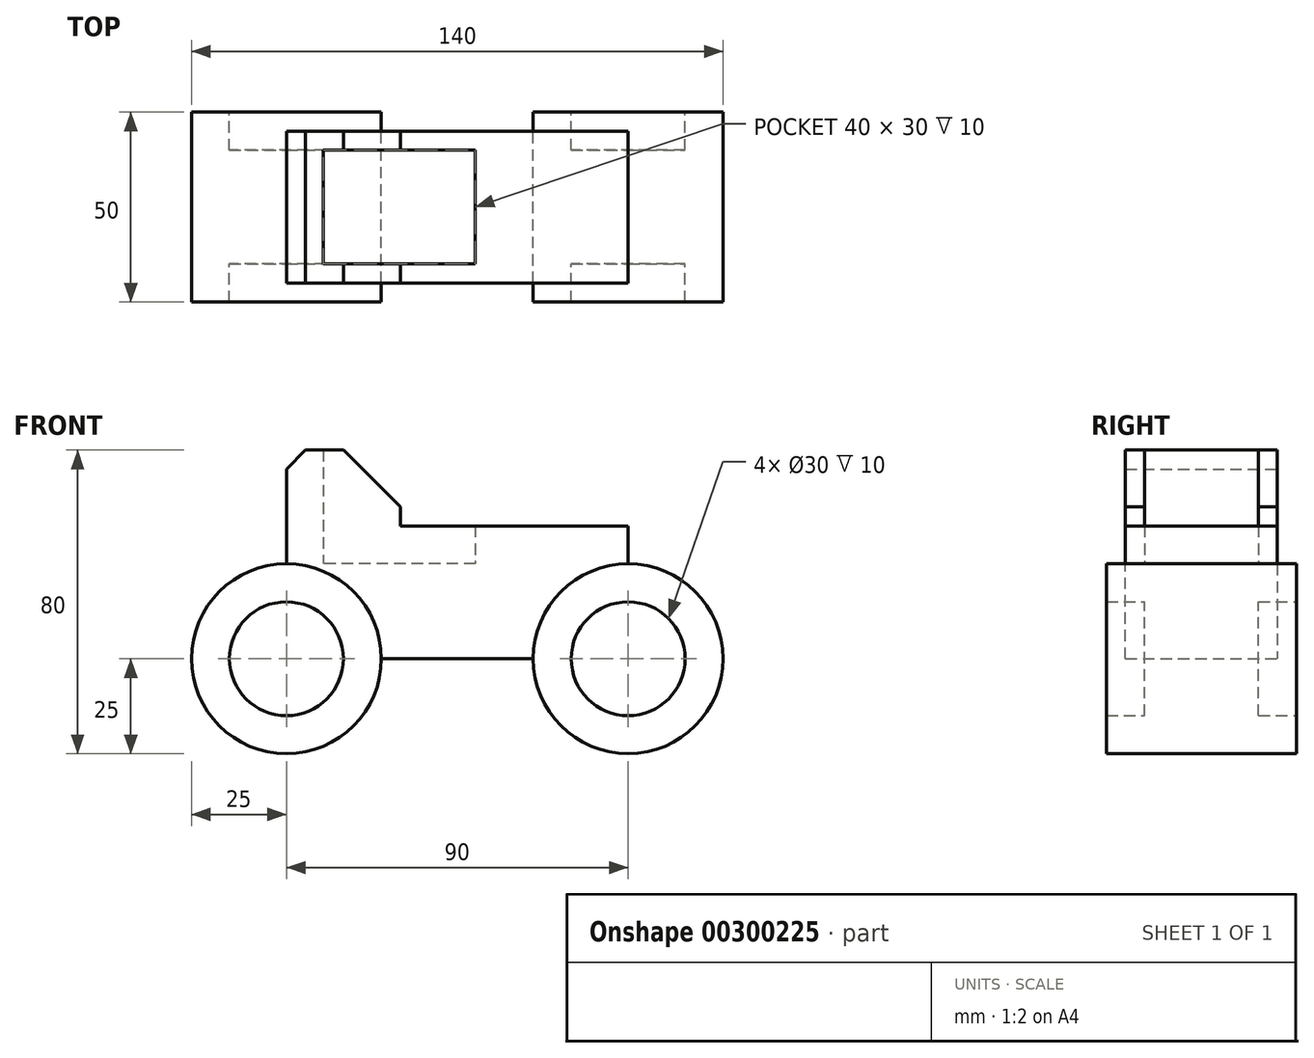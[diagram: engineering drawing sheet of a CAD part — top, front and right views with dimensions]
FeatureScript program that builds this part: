
annotation { "Feature Type Name" : "Feature", "Feature Type Description" : "" }
export const myFeature = defineFeature(function(context is Context, id is Id, definition is map)
    precondition{}
    {
        {
            var Q0;
            Q0=qCreatedBy(makeId("Front.planeOp"),FACE);
            var sketch = newSketch(context, id + "F0", { "sketchPlane" : qUnion([Q0])});
            skLineSegment(sketch, "E0.bottom", {"start": v(45, -17.5) * mm, "end": v(-45, -17.5) * mm});
            skLineSegment(sketch, "E0.top", {"start": v(45, 17.5) * mm, "end": v(-45, 17.5) * mm});
            skLineSegment(sketch, "E0.left", {"start": v(45, -17.5) * mm, "end": v(45, 17.5) * mm});
            skLineSegment(sketch, "E0.right", {"start": v(-45, -17.5) * mm, "end": v(-45, 17.5) * mm});
            skPoint(sketch, "E0.middle", {"position": v(0, 0) * mm});
            skCircle(sketch, "E1", {"center": v(-45, -17.5) * mm, "radius": 15 * mm});
            skCircle(sketch, "E2", {"center": v(-45, -17.5) * mm, "radius": 25 * mm});
            skCircle(sketch, "E3", {"center": v(45, -17.5) * mm, "radius": 15 * mm});
            skCircle(sketch, "E4", {"center": v(45, -17.5) * mm, "radius": 25 * mm});
            skLineSegment(sketch, "E5", {"start": v(-45, 17.5) * mm, "end": v(-45, 37.5) * mm});
            skLineSegment(sketch, "E6", {"start": v(-45, 37.5) * mm, "end": v(-15, 37.5) * mm});
            skLineSegment(sketch, "E7", {"start": v(-15, 37.5) * mm, "end": v(-15, 17.5) * mm});
            skLineSegment(sketch, "E8", {"start": v(-45, 32.5) * mm, "end": v(-40, 37.5) * mm});
            skLineSegment(sketch, "E9", {"start": v(-30, 37.5) * mm, "end": v(-15, 22.5) * mm});
            skSolve(sketch);
        }
        {
            var Q0;
            {var subQ3=sQuery(id+"F0.wireOp",EDGE,"E4");var subQ8=sQuery(id+"F0.wireOp",EDGE,"E0.bottom");var subQ9=makeQuery(id+"F0.imprint","INTERSECT",VERTEX,{"derivedFrom":[subQ8,subQ3]});Q0=makeQuery(id+"F0.imprint","IMPRINT",FACE,{"disambiguationData":[TD([[makeQuery(id+"F0.imprint","IMPRINT",EDGE,{"disambiguationData":[TD([[subQ9,-1.0]])],"derivedFrom":subQ8}),-1.0]])]});}
            var Q1;
            {var subQ4=sQuery(id+"F0.wireOp",EDGE,"E8");Q1=makeQuery(id+"F0.imprint","IMPRINT",FACE,{"disambiguationData":[TD([[makeQuery(id+"F0.imprint","IMPRINT",EDGE,{"derivedFrom":subQ4}),-1.0]])]});}
            extrude(context, id + "F1", {"entities" : qUnion([Q0, Q1]), "endBound" : BoundingType.SYMMETRIC, "depth" : 40 * mm});
        }
        {
            var Q0;
            {var subQ0=sQuery(id+"F0.wireOp",EDGE,"E4");var subQ1=sQuery(id+"F0.wireOp",EDGE,"E0.bottom");var subQ2=makeQuery(id+"F0.imprint","INTERSECT",VERTEX,{"derivedFrom":[subQ1,subQ0]});Q0=makeQuery(id+"F0.imprint","IMPRINT",FACE,{"disambiguationData":[TD([[makeQuery(id+"F0.imprint","IMPRINT",EDGE,{"disambiguationData":[TD([[subQ2,1.0]])],"derivedFrom":subQ1}),1.0]])]});}
            var Q1;
            {var subQ0=sQuery(id+"F0.wireOp",EDGE,"E4");var subQ1=sQuery(id+"F0.wireOp",EDGE,"E0.bottom");var subQ2=makeQuery(id+"F0.imprint","INTERSECT",VERTEX,{"derivedFrom":[subQ1,subQ0]});Q1=makeQuery(id+"F0.imprint","IMPRINT",FACE,{"disambiguationData":[TD([[makeQuery(id+"F0.imprint","IMPRINT",EDGE,{"disambiguationData":[TD([[subQ2,1.0]])],"derivedFrom":subQ1}),-1.0]])]});}
            var Q2;
            {var subQ0=sQuery(id+"F0.wireOp",EDGE,"E2");var subQ1=sQuery(id+"F0.wireOp",EDGE,"E0.bottom");var subQ2=makeQuery(id+"F0.imprint","INTERSECT",VERTEX,{"derivedFrom":[subQ1,subQ0]});Q2=makeQuery(id+"F0.imprint","IMPRINT",FACE,{"disambiguationData":[TD([[makeQuery(id+"F0.imprint","IMPRINT",EDGE,{"disambiguationData":[TD([[subQ2,-1.0]])],"derivedFrom":subQ1}),1.0]])]});}
            var Q3;
            {var subQ0=sQuery(id+"F0.wireOp",EDGE,"E2");var subQ1=sQuery(id+"F0.wireOp",EDGE,"E0.bottom");var subQ2=makeQuery(id+"F0.imprint","INTERSECT",VERTEX,{"derivedFrom":[subQ1,subQ0]});Q3=makeQuery(id+"F0.imprint","IMPRINT",FACE,{"disambiguationData":[TD([[makeQuery(id+"F0.imprint","IMPRINT",EDGE,{"disambiguationData":[TD([[subQ2,-1.0]])],"derivedFrom":subQ1}),-1.0]])]});}
            extrude(context, id + "F2", {"entities" : qUnion([Q0, Q1, Q2, Q3]), "operationType" : NewBodyOperationType.ADD, "endBound" : BoundingType.SYMMETRIC, "depth" : 50 * mm});
        }
        {
            var Q0;
            {var subQ0=sQuery(id+"F0.wireOp",EDGE,"E0.left");var subQ1=sQuery(id+"F0.wireOp",EDGE,"E0.bottom");var subQ2=makeQuery(id+"F0.imprint","INTERSECT",VERTEX,{"derivedFrom":[subQ1,subQ0]});Q0=makeQuery(id+"F0.imprint","IMPRINT",FACE,{"disambiguationData":[TD([[makeQuery(id+"F0.imprint","IMPRINT",EDGE,{"disambiguationData":[TD([[subQ2,-1.0]])],"derivedFrom":subQ1}),1.0]])]});}
            var Q1;
            {var subQ0=sQuery(id+"F0.wireOp",EDGE,"E0.left");var subQ1=sQuery(id+"F0.wireOp",EDGE,"E0.bottom");var subQ2=makeQuery(id+"F0.imprint","INTERSECT",VERTEX,{"derivedFrom":[subQ1,subQ0]});Q1=makeQuery(id+"F0.imprint","IMPRINT",FACE,{"disambiguationData":[TD([[makeQuery(id+"F0.imprint","IMPRINT",EDGE,{"disambiguationData":[TD([[subQ2,-1.0]])],"derivedFrom":subQ1}),-1.0]])]});}
            var Q2;
            {var subQ0=sQuery(id+"F0.wireOp",EDGE,"E0.right");var subQ1=sQuery(id+"F0.wireOp",EDGE,"E0.bottom");var subQ2=makeQuery(id+"F0.imprint","INTERSECT",VERTEX,{"derivedFrom":[subQ1,subQ0]});Q2=makeQuery(id+"F0.imprint","IMPRINT",FACE,{"disambiguationData":[TD([[makeQuery(id+"F0.imprint","IMPRINT",EDGE,{"disambiguationData":[TD([[subQ2,1.0]])],"derivedFrom":subQ1}),1.0]])]});}
            var Q3;
            {var subQ0=sQuery(id+"F0.wireOp",EDGE,"E0.right");var subQ1=sQuery(id+"F0.wireOp",EDGE,"E0.bottom");var subQ2=makeQuery(id+"F0.imprint","INTERSECT",VERTEX,{"derivedFrom":[subQ1,subQ0]});Q3=makeQuery(id+"F0.imprint","IMPRINT",FACE,{"disambiguationData":[TD([[makeQuery(id+"F0.imprint","IMPRINT",EDGE,{"disambiguationData":[TD([[subQ2,1.0]])],"derivedFrom":subQ1}),-1.0]])]});}
            extrude(context, id + "F3", {"entities" : qUnion([Q0, Q1, Q2, Q3]), "operationType" : NewBodyOperationType.ADD, "endBound" : BoundingType.SYMMETRIC, "depth" : 30 * mm});
        }
        {
            var Q0;
            Q0=qCreatedBy(makeId("Top.planeOp"),FACE);
            var sketch = newSketch(context, id + "F4", { "sketchPlane" : qUnion([Q0])});
            skLineSegment(sketch, "E10", {"start": v(-35.24, 0) * mm, "end": v(-35.24, 15) * mm});
            skLineSegment(sketch, "E11", {"start": v(-35.24, 15) * mm, "end": v(4.76, 15) * mm});
            skLineSegment(sketch, "E12", {"start": v(4.76, 15) * mm, "end": v(4.76, -15) * mm});
            skLineSegment(sketch, "E13", {"start": v(4.76, -15) * mm, "end": v(-35.24, -15) * mm});
            skLineSegment(sketch, "E14", {"start": v(-35.24, -15) * mm, "end": v(-35.24, 0) * mm});
            skLineSegment(sketch, "E15", {"start": v(-35.24, 15) * mm, "end": v(-35.24, -15) * mm});
            skLineSegment(sketch, "E16", {"start": v(4.76, -15) * mm, "end": v(4.76, 15) * mm});
            skLineSegment(sketch, "E17", {"start": v(-35.24, -15) * mm, "end": v(4.76, -15) * mm});
            skSolve(sketch);
        }
        {
            var Q0;
            Q0 = qSketchRegion(id + "F4", true);
            var Q1;
            Q1=sQuery(id+"F4.wireOp",EDGE,"E15");
            var Q2;
            Q2=sQuery(id+"F4.wireOp",EDGE,"E11");
            var Q3;
            Q3=sQuery(id+"F4.wireOp",EDGE,"E16");
            var Q4;
            Q4=sQuery(id+"F4.wireOp",EDGE,"E13");
            extrude(context, id + "F5", {"entities" : qUnion([Q0]), "operationType" : NewBodyOperationType.REMOVE, "surfaceEntities" : qUnion([Q1, Q2, Q3, Q4]), "depth" : 37.5 * mm, "hasSecondDirection" : true, "secondDirectionOppositeDirection" : false, "secondDirectionDepth" : 7.5 * mm});
        }
    });
